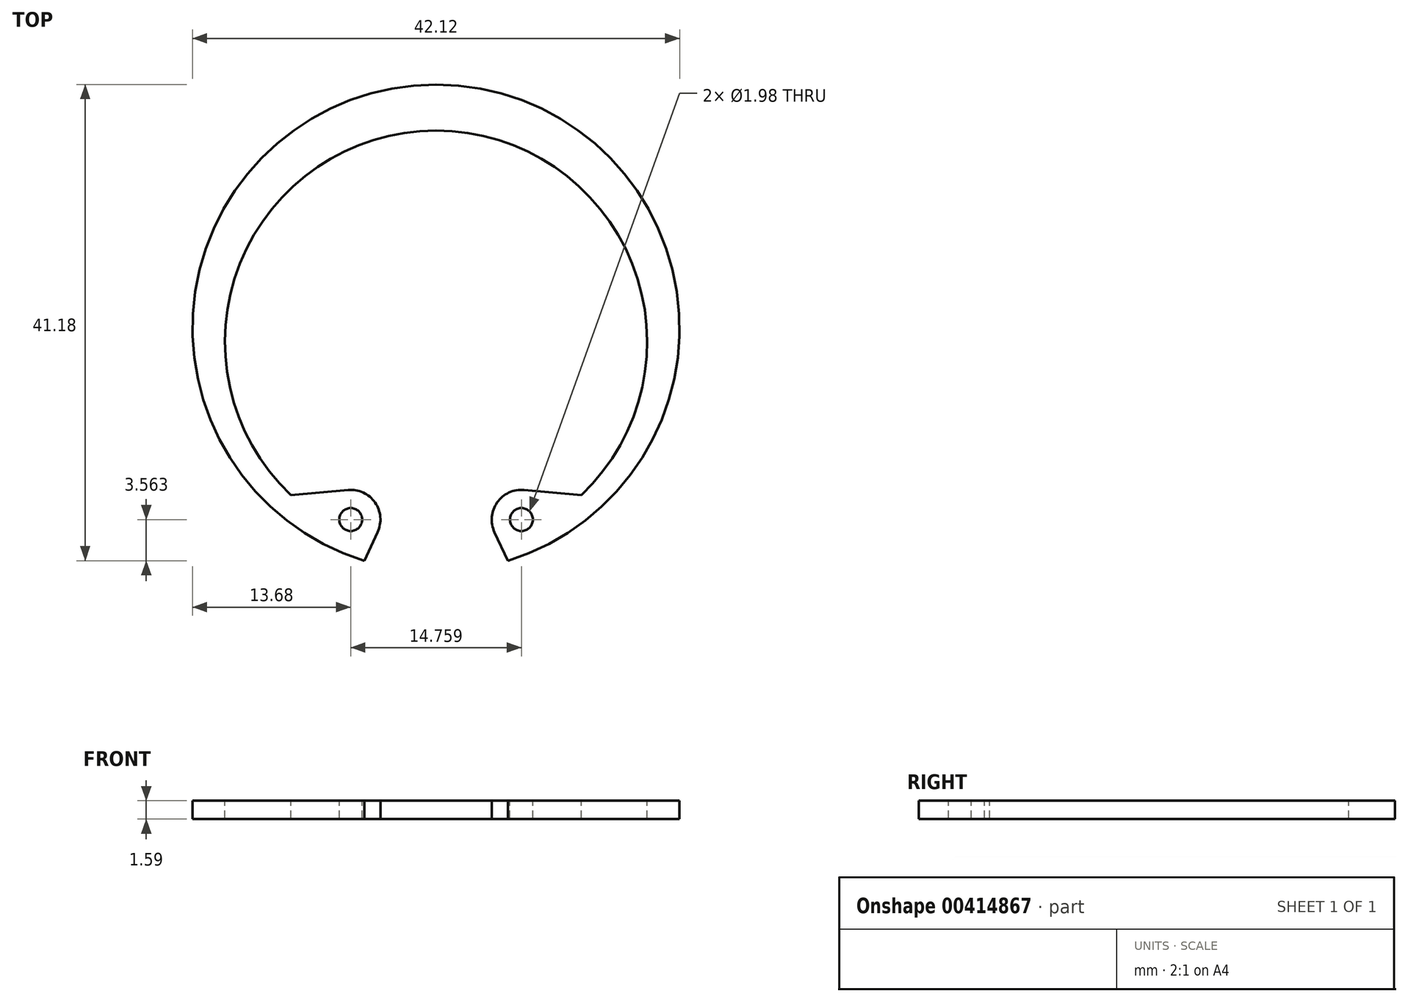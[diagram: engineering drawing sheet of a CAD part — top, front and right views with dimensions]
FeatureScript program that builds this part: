
annotation { "Feature Type Name" : "Feature", "Feature Type Description" : "" }
export const myFeature = defineFeature(function(context is Context, id is Id, definition is map)
    precondition{}
    {
        {
            var Q0;
            Q0=qCreatedBy(makeId("Top.planeOp"),FACE);
            var sketch = newSketch(context, id + "F0", { "sketchPlane" : qUnion([Q0])});
            skArc(sketch, "E0", {"start": v(42.85, -21.33) * mm, "mid": v(36.64, 19.85) * mm, "end": v(30.43, -21.33) * mm});
            skCircle(sketch, "E1", {"center": v(29.26, -17.77) * mm, "radius": 1 * mm});
            skLineSegment(sketch, "E2", {"start": v(30.43, -21.33) * mm, "end": v(31.58, -18.85) * mm});
            skArc(sketch, "E3", {"start": v(31.58, -18.85) * mm, "mid": v(31.36, -16.3) * mm, "end": v(29.03, -15.21) * mm});
            skLineSegment(sketch, "E4", {"start": v(29.03, -15.21) * mm, "end": v(24.08, -15.64) * mm});
            skCircle(sketch, "E5", {"center": v(44.02, -17.77) * mm, "radius": 1 * mm});
            skLineSegment(sketch, "E6", {"start": v(42.85, -21.33) * mm, "end": v(41.7, -18.85) * mm});
            skArc(sketch, "E7", {"start": v(44.24, -15.21) * mm, "mid": v(41.92, -16.3) * mm, "end": v(41.7, -18.85) * mm});
            skLineSegment(sketch, "E8", {"start": v(44.24, -15.21) * mm, "end": v(49.2, -15.64) * mm});
            skArc(sketch, "E9", {"start": v(49.2, -15.64) * mm, "mid": v(36.64, 15.86) * mm, "end": v(24.08, -15.64) * mm});
            skLineSegment(sketch, "E10", {"start": v(36.64, -1.2) * mm, "end": v(36.64, 19.85) * mm, "construction": true});
            skSolve(sketch);
        }
        {
            var Q0;
            Q0 = qSketchRegion(id + "F0", true);
            extrude(context, id + "F1", {"entities" : qUnion([Q0]), "oppositeDirection" : true, "depth" : 1.59 * mm});
        }
        {
            var Q0;
            Q0=makeQuery(id+"F1.opExtrude","CAP_EDGE",EDGE,{"disambiguationData":[OSD([sQuery(id+"F0.wireOp",EDGE,"E0")])],"isStart":true});
            cPoint(context, id + "F2", {"entities" : qUnion([Q0]), "parameter" : 0.5});
        }
        {
            var Q0;
            Q0=makeQuery(id+"F1.opExtrude","SWEPT_BODY",BODY,{"disambiguationData":[OSD([sQuery(id+"F0.wireOp",EDGE,"E0"),sQuery(id+"F0.wireOp",EDGE,"E1"),sQuery(id+"F0.wireOp",EDGE,"E2"),sQuery(id+"F0.wireOp",EDGE,"E3"),sQuery(id+"F0.wireOp",EDGE,"E4"),sQuery(id+"F0.wireOp",EDGE,"E5"),sQuery(id+"F0.wireOp",EDGE,"E6"),sQuery(id+"F0.wireOp",EDGE,"E7"),sQuery(id+"F0.wireOp",EDGE,"E8"),sQuery(id+"F0.wireOp",EDGE,"E9")])]});
            var Q1;
            Q1 = qCreatedBy(id + "F2" ,VERTEX);
            var Q2;
            Q2=qCreatedBy(makeId("Origin.pointOp"),VERTEX);
            transform(context, id + "F3", {"entities" : qUnion([Q0]), "transformType" : TransformType.TRANSLATION_ENTITY, "oppositeDirectionEntity" : false, "transformLine" : qUnion([Q1, Q2]), "makeCopy" : false});
        }
        {
            var Q0;
            Q0=makeQuery(id+"F1.opExtrude","SWEPT_BODY",BODY,{"disambiguationData":[OSD([sQuery(id+"F0.wireOp",EDGE,"E0"),sQuery(id+"F0.wireOp",EDGE,"E1"),sQuery(id+"F0.wireOp",EDGE,"E2"),sQuery(id+"F0.wireOp",EDGE,"E3"),sQuery(id+"F0.wireOp",EDGE,"E4"),sQuery(id+"F0.wireOp",EDGE,"E5"),sQuery(id+"F0.wireOp",EDGE,"E6"),sQuery(id+"F0.wireOp",EDGE,"E7"),sQuery(id+"F0.wireOp",EDGE,"E8"),sQuery(id+"F0.wireOp",EDGE,"E9")])]});
            transform(context, id + "F4", {"entities" : qUnion([Q0]), "transformType" : TransformType.TRANSLATION_3D, "dx" : 0 * mm, "dy" : 21.06 * mm, "dz" : 0 * mm, "makeCopy" : false});
        }
    });
